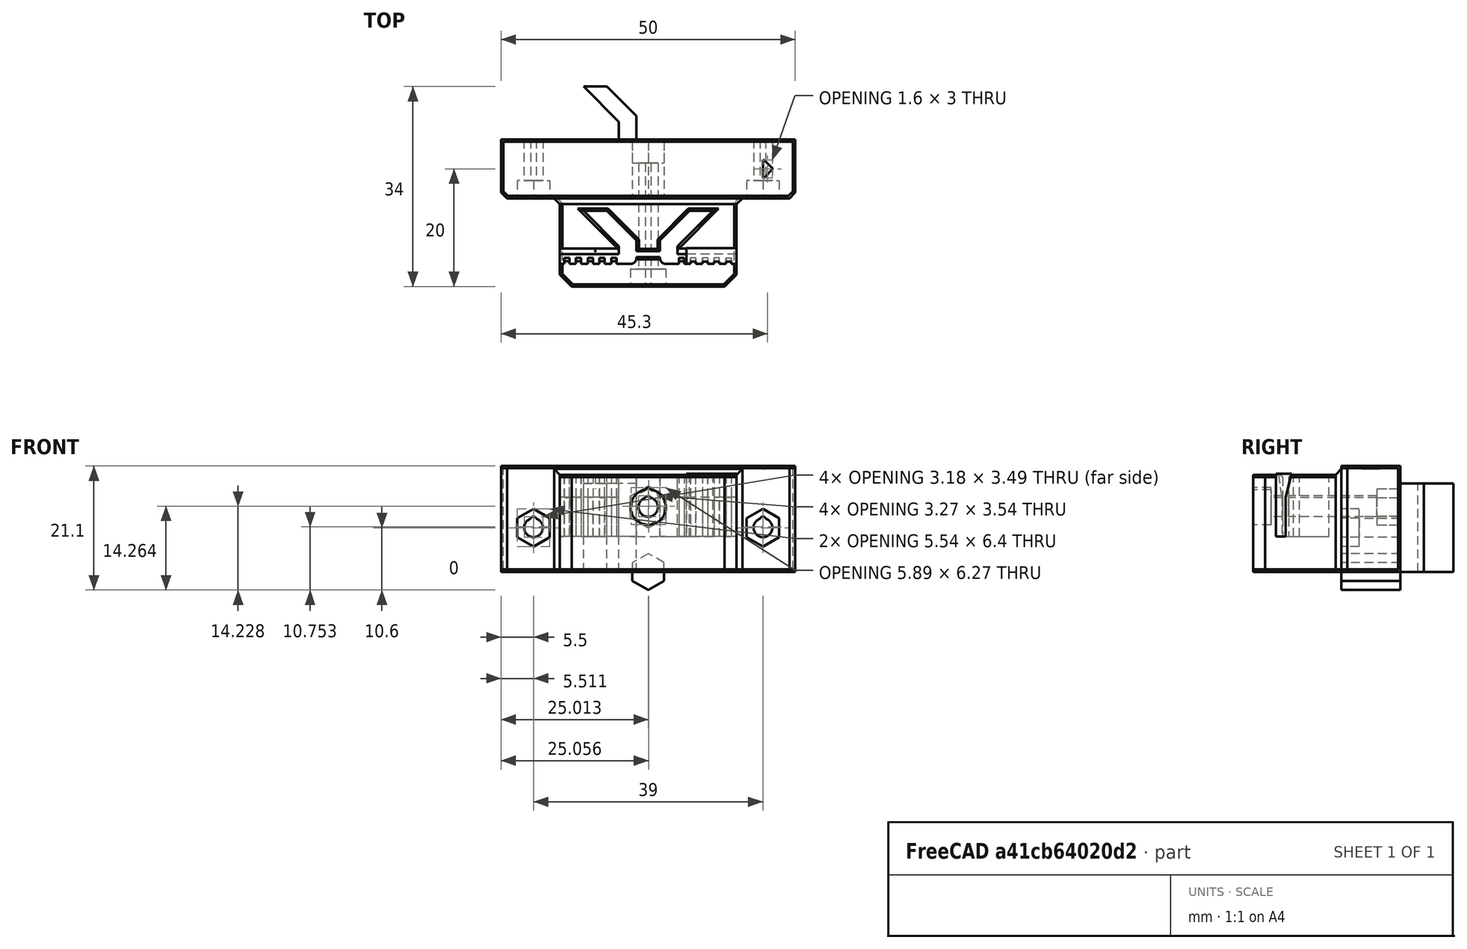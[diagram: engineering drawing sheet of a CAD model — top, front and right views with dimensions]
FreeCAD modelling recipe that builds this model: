
FCSTD DOCUMENT  (FreeCAD 0.18R14555 (Git shallow))
Label: y-belt-holder-10mm-lower
License: All rights reserved
LicenseURL: http://en.wikipedia.org/wiki/All_rights_reserved
objects: Part::Cut×13, Part::Feature×11, Part::MultiFuse×9, Part::Cylinder×8, Part::Box×7, Part::Chamfer×6, Sketcher::SketchObject×2, PartDesign::Pad×2, PartDesign::Body×2, Mesh::Feature×1, Part::Fillet×1, Part::Mirroring×1
note: 64 computed .brp shape members not serialized (recipe doc carries the construction recipe); baked Part::Feature solids carry a one-line shape summary decoded from their .brp

FEATURE [Part::Box] Box  label="Cube"
  AttacherType = Attacher::AttachEngine3D
  Height = 18
  Length = 50
  Placement = pos=(-25,-10,0) rot=(0,0,1;0rad)
  Width = 10
FEATURE [Part::Box] Box001  label="Cube001"
  AttacherType = Attacher::AttachEngine3D
  Height = 16.5
  Length = 30
  Placement = pos=(-15,-25,0) rot=(0,0,1;0rad)
  Width = 16
FEATURE [Part::Cylinder] Cylinder008
  Angle = 360
  AttacherType = Attacher::AttachEngine3D
  Height = 18
  Placement = pos=(-19.5,2e-15,7.5) rot=(1,0,0;1.5708rad)
  Radius = 1.6
FEATURE [Part::Cylinder] Cylinder009
  Angle = 360
  AttacherType = Attacher::AttachEngine3D
  Height = 18
  Placement = pos=(19.5,2e-15,7.5) rot=(1,0,0;1.5708rad)
  Radius = 1.6
FEATURE [Part::MultiFuse] Fusion005
  Shapes = -> [Cylinder008,Cylinder009]
FEATURE [Part::Feature] Body001
  Placement = pos=(-19.5,0,7.5) rot=(0,0,1;0rad)
  shape: bbox 5.543 x 3 x 6.4 mm, 8 faces (baked)
FEATURE [Part::Feature] Body002
  Placement = pos=(19.5,0,7.5) rot=(0,0,1;0rad)
  shape: bbox 5.543 x 3 x 6.4 mm, 8 faces (baked)
FEATURE [Part::MultiFuse] Fusion006
  Placement = pos=(0,-7,0) rot=(0,0,1;0rad)
  Shapes = -> [Body002,Body001]
FEATURE [Part::Cylinder] Cylinder010
  Angle = 360
  AttacherType = Attacher::AttachEngine3D
  Height = 10
  Placement = pos=(-19.5,2e-15,7.5) rot=(1,0,0;1.5708rad)
  Radius = 0.5
FEATURE [Part::Cylinder] Cylinder011
  Angle = 360
  AttacherType = Attacher::AttachEngine3D
  Height = 10
  Placement = pos=(19.5,2e-15,7.5) rot=(1,0,0;1.5708rad)
  Radius = 0.5
FEATURE [Part::MultiFuse] Fusion007
  Placement = pos=(0,0,1.4) rot=(0,0,1;0rad)
  Shapes = -> [Cylinder010,Cylinder011]
FEATURE [Part::MultiFuse] Fusion008006  label="mounting-screw"
  Shapes = -> [Fusion005,Fusion006,Fusion007]
FEATURE [Part::Box] Box005  label="Cube005"
  AttacherType = Attacher::AttachEngine3D
  Height = 0.5
  Length = 1.6
  Placement = pos=(0,4,0) rot=(0,0,1;0rad)
  Width = 3
FEATURE [Part::Chamfer] Chamfer  label="indicator"
  Base = -> Box005
  Edges = 2 edges r=1.4: [Edge5,Edge7]
  Placement = pos=(19.5,-10.5,17.5) rot=(0,0,1;0rad)
FEATURE [Part::Feature] Grand_Jaagub_Leelo001_solid001  label="Grand_Jaagub_Leelo001 (Solid)001"
  Placement = pos=(0,0,0) rot=(0,0,1;3.14159rad)
  shape: bbox 52 x 26 x 14.6 mm, 1753 faces (baked)
FEATURE [Part::Box] Box006  label="Cube006"
  AttacherType = Attacher::AttachEngine3D
  Height = 13.59
  Length = 8.5
  Placement = pos=(7,-7,1) rot=(0,0,1;0rad)
  Width = 5
FEATURE [Part::Cut] Cut004  label="belt-slot"
  Base = -> Box006
  Placement = pos=(-0.5,-14.6,2.1) rot=(0,0,1;0rad)
  Tool = -> Grand_Jaagub_Leelo001_solid001
FEATURE [Mesh::Feature] y_belt_holder
  Placement = pos=(1.1e-15,9,0) rot=(0,0,1;3.14159rad)
FEATURE [Part::MultiFuse] Fusion
  Shapes = -> [Box,Box001]
FEATURE [Part::Cut] Cut
  Base = -> Fusion
  Tool = -> Fusion008006
FEATURE [Part::Feature] Cut004001  label="belt-slot001"
  Placement = pos=(-0.5,-14.6,2.1) rot=(0,0,1;0rad)
  shape: bbox 8.5 x 2.672 x 10.69 mm, 28 faces (baked)
FEATURE [Part::Feature] Cut004002  label="belt-slot002"
  Placement = pos=(-8.5,-14.6,2.1) rot=(0,0,1;0rad)
  shape: bbox 8.5 x 2.672 x 10.69 mm, 28 faces (baked)
FEATURE [Part::Feature] Cut004003  label="belt-slot003"
  Placement = pos=(-16,-14.6,2.1) rot=(0,0,1;0rad)
  shape: bbox 8.5 x 2.672 x 10.69 mm, 28 faces (baked)
FEATURE [Part::Feature] Cut004004  label="belt-slot004"
  Placement = pos=(-22,-14.6,2.1) rot=(0,0,1;0rad)
  shape: bbox 8.5 x 2.672 x 10.69 mm, 28 faces (baked)
FEATURE [Part::MultiFuse] Fusion008007
  Shapes = -> [Cut004003,Cut004004]
FEATURE [Part::MultiFuse] Fusion008008
  Shapes = -> [Cut004002,Cut004001]
FEATURE [Part::Box] Box007  label="Cube007"
  AttacherType = Attacher::AttachEngine3D
  Height = 11
  Length = 10
  Placement = pos=(-5,-21.15,6) rot=(0,0,1;0rad)
  Width = 10
FEATURE [Part::Box] Box008  label="Cube008"
  AttacherType = Attacher::AttachEngine3D
  Height = 11
  Length = 10
  Placement = pos=(-5,-21.15,6) rot=(0,0,1;0rad)
  Width = 10
FEATURE [Part::Cut] Cut004005
  Base = -> Fusion008007
  Tool = -> Box007
FEATURE [Part::Cut] Cut004006
  Base = -> Fusion008008
  Tool = -> Box008
FEATURE [Part::Cut] Cut004007
  Base = -> Cut
  Tool = -> Chamfer
FEATURE [Sketcher::SketchObject] Sketch
  MapMode = 5
  Support = -> [XY_Plane]
  sketch-geometry (6):
    g0: LineSegment StartX=-2 StartY=0 StartZ=0 EndX=-5 EndY=0 EndZ=0
    g1: LineSegment StartX=-2 StartY=0 StartZ=0 EndX=-2 EndY=4 EndZ=0
    g2: LineSegment StartX=-5 StartY=0 StartZ=0 EndX=-5 EndY=3 EndZ=0
    g3: LineSegment StartX=-5 StartY=3 StartZ=0 EndX=-11 EndY=9 EndZ=0
    g4: LineSegment StartX=-2 StartY=4 StartZ=0 EndX=-7 EndY=9 EndZ=0
    g5: LineSegment StartX=-11 StartY=9 StartZ=0 EndX=-7 EndY=9 EndZ=0
  constraints (11):
    c: PointOnObject(g0,g-1)
    c: Horizontal(g0)
    c: Coincident(g1,g0)
    c: Vertical(g1)
    c: Coincident(g2,g0)
    c: Vertical(g2)
    c: Coincident(g3,g2)
    c: Coincident(g4,g1)
    c: Coincident(g5,g3)
    c: Coincident(g5,g4)
    c: Horizontal(g5)
FEATURE [PartDesign::Pad] Pad
  Length = 15
  Length2 = 100
  Profile = -> Sketch
  Type = 0
FEATURE [PartDesign::Body] Body
  Group = -> [Sketch,Pad]
  Origin = -> Origin
  Tip = -> Pad
FEATURE [Part::Feature] Body003
  Placement = pos=(0,-21.15,6) rot=(0,0,1;0rad)
  shape: bbox 9 x 9 x 15 mm, 8 faces (baked)
FEATURE [Part::Fillet] Fillet
  Base = -> Body003
  Edges = 1 edges r=1: [Edge1]
FEATURE [Part::Feature] Fillet001
  shape: bbox 9 x 9 x 15 mm, 9 faces (baked)
FEATURE [Part::MultiFuse] Fusion008009
  Shapes = -> [Cut004005,Fillet]
FEATURE [Part::Cut] Cut004008
  Base = -> Cut004007
  Tool = -> Fusion008009
FEATURE [Part::Mirroring] Part__Mirroring  label="Fillet001 (Mirror #1)"
  Base = (0,0,0)
  Normal = (1,0,0)
  Source = -> Fillet001
FEATURE [Part::MultiFuse] Fusion008010
  Shapes = -> [Cut004006,Part__Mirroring]
FEATURE [Part::Cut] Cut004009
  Base = -> Cut004008
  Tool = -> Fusion008010
FEATURE [Part::Cylinder] Cylinder
  Angle = 360
  AttacherType = Attacher::AttachEngine3D
  Height = 3
  Placement = pos=(0,-22,11) rot=(1,0,0;1.5708rad)
  Radius = 3
FEATURE [Part::Cylinder] Cylinder012
  Angle = 360
  AttacherType = Attacher::AttachEngine3D
  Height = 28
  Placement = pos=(0,2.3e-15,12.4) rot=(1,0,0;1.5708rad)
  Radius = 0.5
FEATURE [Part::Cylinder] Cylinder013
  Angle = 360
  AttacherType = Attacher::AttachEngine3D
  Height = 28
  Placement = pos=(0,2e-15,11) rot=(1,0,0;1.5708rad)
  Radius = 1.65
FEATURE [Part::Cut] Cut004010
  Base = -> Cut004009
  Tool = -> Cylinder013
FEATURE [Part::Cut] Cut004011
  Base = -> Cut004010
  Tool = -> Cylinder012
FEATURE [Part::Cylinder] Cylinder014
  Angle = 360
  AttacherType = Attacher::AttachEngine3D
  Height = 3
  Placement = pos=(0,-22,13.8) rot=(1,0,0;1.5708rad)
  Radius = 0.5
FEATURE [Part::Cut] Cut004012
  Base = -> Cut004011
  Tool = -> Cylinder
FEATURE [Part::Cut] Cut004013
  Base = -> Cut004012
  Tool = -> Cylinder014
FEATURE [Part::Box] Box009  label="Cube009"
  AttacherType = Attacher::AttachEngine3D
  Height = 13
  Length = 6
  Placement = pos=(-3,-20,6) rot=(0,0,1;0rad)
  Width = 1
FEATURE [Part::Cut] Cut004014
  Base = -> Cut004013
  Tool = -> Box009
FEATURE [Part::Chamfer] Chamfer001
  Base = -> Cut004014
  Edges = 12 edges r=0.4: [Edge56,Edge57,Edge58,Edge59,Edge60,Edge68,Edge69,Edge70,Edge71,Edge72,Edge73,Edge163]
FEATURE [Sketcher::SketchObject] Sketch001
  MapMode = 5
  Placement = pos=(0,0,0) rot=(1,0,0;1.5708rad)
  Support = -> [XZ_Plane001]
  sketch-geometry (7):
    g0: LineSegment StartX=0 StartY=-3.1 StartZ=0 EndX=2.68468 EndY=-1.55 EndZ=0
    g1: LineSegment StartX=2.68468 StartY=-1.55 StartZ=0 EndX=2.68468 EndY=1.55 EndZ=0
    g2: LineSegment StartX=2.68468 StartY=1.55 StartZ=0 EndX=4e-16 EndY=3.1 EndZ=0
    g3: LineSegment StartX=4e-16 StartY=3.1 StartZ=0 EndX=-2.68468 EndY=1.55 EndZ=0
    g4: LineSegment StartX=-2.68468 StartY=1.55 StartZ=0 EndX=-2.68468 EndY=-1.55 EndZ=0
    g5: LineSegment StartX=-2.68468 StartY=-1.55 StartZ=0 EndX=0 EndY=-3.1 EndZ=0
    g6: Circle [constr] CenterX=0 CenterY=0 CenterZ=0 NormalX=0 NormalY=0 NormalZ=1 AngleXU=0 Radius=3.1
  constraints (15):
    c: Coincident(g0,g1)
    c: Coincident(g1,g2)
    c: Coincident(g2,g3)
    c: Coincident(g3,g4)
    c: Coincident(g4,g5)
    c: Coincident(g5,g0)
    c: Equal(g0, g1-g5) x5
    c: PointOnObject(g0,g6)
    c: PointOnObject(g1,g6)
    c: PointOnObject(g2,g6)
    c: PointOnObject(g3,g6)
    c: PointOnObject(g4,g6)
    c: PointOnObject(g5,g6)
    c: Coincident(g6,g-1)
    c: PointOnObject(g5,g-2)
FEATURE [PartDesign::Pad] Pad001
  Length = 10
  Length2 = 100
  Placement = pos=(0,0,0) rot=(1,0,0;1.5708rad)
  Profile = -> Sketch001
  Type = 0
FEATURE [PartDesign::Body] Body004
  Group = -> [Sketch001,Pad001]
  Origin = -> Origin001
  Tip = -> Pad001
FEATURE [Part::Feature] Body004001  label="Body005"
  Placement = pos=(0,6,11) rot=(0,0,1;0rad)
  shape: bbox 5.369 x 10 x 6.2 mm, 8 faces (baked)
FEATURE [Part::Cut] Cut004015
  Base = -> Chamfer001
  Tool = -> Body004001
FEATURE [Part::Chamfer] Chamfer002
  Base = -> Cut004015
  Edges = 2 edges r=2: [Edge42,Edge72]
FEATURE [Part::Chamfer] Chamfer003
  Base = -> Chamfer002
  Edges = 5 edges r=1: [Edge6,Edge89,Edge91,Edge92,Edge93]
FEATURE [Part::Feature] Chamfer003001  label="Chamfer004"
  shape: bbox 50 x 25 x 18 mm, 150 faces (baked)
FEATURE [Part::Chamfer] Chamfer003002
  Base = -> Chamfer003001
  Edges = 29 edges r=0.4: [Edge1,Edge5,Edge7,Edge8,Edge14,Edge17,Edge18,Edge24,Edge27,Edge29,Edge49,Edge51,Edge101,Edge106,Edge107,Edge109,Edge112,Edge273,Edge275,Edge276,Edge277,Edge278,Edge279,Edge280,Edge281,Edge294,Edge296,Edge297,Edge298]
FEATURE [Part::Chamfer] Chamfer003003
  Base = -> Chamfer003002
  Edges = 6 edges r=0.4: [Edge463,Edge464,Edge465,Edge466,Edge467,Edge468]
